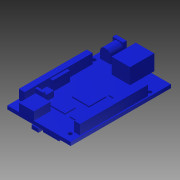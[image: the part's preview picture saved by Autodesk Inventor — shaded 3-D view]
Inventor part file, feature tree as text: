
AUTODESK INVENTOR PART (.ipt)
format: ipt  version: 2013 (Build 170138000, 138)  size: 267,776 bytes
history: native  units: mm
features: sketch x14, extrude x13, other x1, hole x1, fillet x1
ambient origin geometry x1: Origin
feature tree (30):
  other  "ソリッド1"
  extrude  "押し出し1"  Depth=87.0mm
  hole  "穴1"  [1 undecoded]
  extrude  "押し出し2"  Depth=27.5mm
  extrude  "押し出し3"  Depth=43.5mm
  extrude  "押し出し4"  Depth=3.0mm TaperAngle=0.0deg
  extrude  "押し出し5"  Depth=3.2mm
  extrude  "押し出し6"  Depth=48.5mm
  extrude  "押し出し7"  Depth=42.0mm
  extrude  "押し出し8"  Depth=21.0mm
  extrude  "押し出し10"  Depth=24.25mm
  extrude  "押し出し11"  Depth=66.0mm
  extrude  "押し出し13"  Depth=66.0mm
  extrude  "押し出し14"  Depth=15.0mm
  extrude  "押し出し15"  Depth=15.0mm
  fillet  "フィレット1"  Radius=5.0mm
  sketch  "スケッチ1"
  sketch  "スケッチ2"
  sketch  "スケッチ3"
  sketch  "スケッチ4"
  sketch  "スケッチ5"
  sketch  "スケッチ6"
  sketch  "スケッチ7"
  sketch  "スケッチ8"
  sketch  "スケッチ9"
  sketch  "スケッチ10"
  sketch  "スケッチ11"
  sketch  "スケッチ12"
  sketch  "スケッチ13"
  sketch  "スケッチ14"
note: 1 required parameter value undecoded (feature->parameter linkage not recoverable at this tier; creation-order binding heuristic only, values carry confidence <= 0.55)
